# Revit family: Chair-Soft_Seating-Allermuir-Stirling-SLW02
name_source: partatom
category: Furniture
revit_build: Autodesk Revit MEP 2012 (Build: 20110309_2315)
units: mm (PartAtom-declared; Revit-internal decimal feet)

## types (1)
- SLW02
    04 CSI = 12 51 00
    95 CSI = 12510
    Arms Height = 21 77/128"
    Assembly Code = E2020200
    Base = Metal - Allermuir - Polished Aluminum
    Brochure URL = http://www.allermuir.net
    CAD Blocks URL = http://www.allermuir.net
    Color Availability = See price list for material options
    Default Elevation = 48"
    Fabric Spec Sheets = http://www.allermuir.net
    Manufacturer = Allermuir
    Manufacturer Fax = (419) 887 5805
    Model = SLW02
    Overall Depth = 36 51/256"
    Overall Height = 35"
    Overall Width = 76"
    Plastic Arms in Black = No
    Plastic glides = Yes
    Plugin Data URL = http://products.ecoscorecard.com
http://products.ecoscorecard.com
    Pricing URL = http://www.allermuir.net
    Product Line = Stirling
    Product Page URL = http://www.allermuir.net
    Seat Depth = 23 1/2"
    Seat Height = 18"
    Seat Width = 52 51/128"
    Seat or Top = Fabric - Allermuir - Silcoates
    Specifications URL = http://www.allermuir.net
    Stacks = No
    Subcategory = Soft Seating
    Tubular Steel Legs = No
    URL = http://www.allermuir.net
    Upholstered Back = Yes
    Weight = 279.00 lb
    ecoScorecard Product Page = http://products.ecoscorecard.com
    ecoScorecard_data = http://thesenatorgroup.ecoscorecard.com

## geometry (parser evidence)
native form markers: Blend x34, Sweep x5
no freeform markers — native parametric forms only
